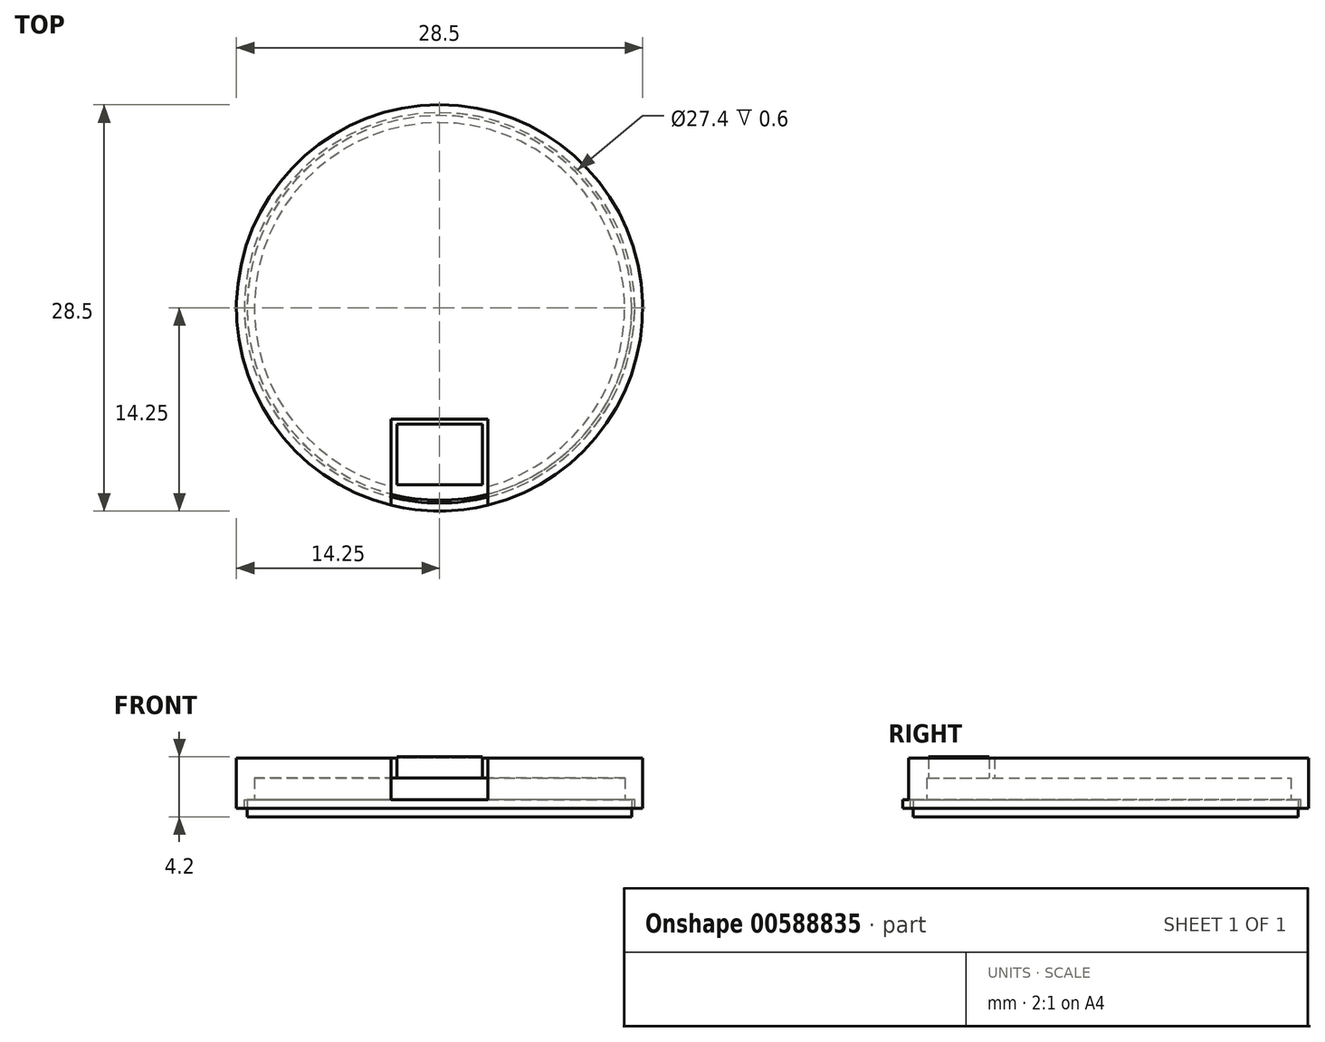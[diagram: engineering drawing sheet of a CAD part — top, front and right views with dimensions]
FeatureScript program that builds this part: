
annotation { "Feature Type Name" : "Feature", "Feature Type Description" : "" }
export const myFeature = defineFeature(function(context is Context, id is Id, definition is map)
    precondition{}
    {
        {
            var Q0;
            Q0=qCreatedBy(makeId("Top.planeOp"),FACE);
            var sketch = newSketch(context, id + "F0", { "sketchPlane" : qUnion([Q0])});
            skCircle(sketch, "E0", {"center": v(0, 0) * mm, "radius": 13.5 * mm});
            skLineSegment(sketch, "E1.bottom", {"start": v(3, -12.42) * mm, "end": v(-3, -12.42) * mm});
            skLineSegment(sketch, "E1.top", {"start": v(3, -8.17) * mm, "end": v(-3, -8.17) * mm});
            skLineSegment(sketch, "E1.left", {"start": v(3, -12.42) * mm, "end": v(3, -8.17) * mm});
            skLineSegment(sketch, "E1.right", {"start": v(-3, -12.42) * mm, "end": v(-3, -8.17) * mm});
            skPoint(sketch, "E1.middle", {"position": v(0, -10.3) * mm});
            skSolve(sketch);
        }
        {
            var Q0;
            Q0 = qSketchRegion(id + "F0", true);
            var Q1;
            Q1=makeQuery(id+"F0.imprint","IMPRINT",FACE,{"disambiguationData":[TD([[makeQuery(id+"F0.imprint","IMPRINT",EDGE,{"derivedFrom":sQuery(id+"F0.wireOp",EDGE,"E1.bottom")}),-1.0]])]});
            extrude(context, id + "F1", {"entities" : qUnion([Q0, Q1]), "depth" : 1.2 * mm, "offsetDistance" : 25 * mm});
        }
        {
            var Q0;
            Q0=makeQuery(id+"F0.imprint","IMPRINT",FACE,{"disambiguationData":[TD([[makeQuery(id+"F0.imprint","IMPRINT",EDGE,{"derivedFrom":sQuery(id+"F0.wireOp",EDGE,"E1.bottom")}),-1.0]])]});
            extrude(context, id + "F2", {"entities" : qUnion([Q0]), "operationType" : NewBodyOperationType.ADD, "depth" : 4.2 * mm, "offsetDistance" : 25 * mm});
        }
        {
            var Q0;
            Q0=makeQuery(id+"F1.opExtrude","CAP_FACE",FACE,{"disambiguationData":[OSD([sQuery(id+"F0.wireOp",EDGE,"E0")])],"isStart":false});
            var sketch = newSketch(context, id + "F3", { "sketchPlane" : qUnion([Q0])});
            skCircle(sketch, "E2", {"center": v(0, 0) * mm, "radius": 14.25 * mm});
            skCircle(sketch, "E3", {"center": v(0, 0) * mm, "radius": 13.7 * mm});
            skLineSegment(sketch, "E4.bottom", {"start": v(3.4, -12.8) * mm, "end": v(-3.4, -12.8) * mm});
            skLineSegment(sketch, "E4.top", {"start": v(3.4, -7.8) * mm, "end": v(-3.4, -7.8) * mm});
            skLineSegment(sketch, "E4.left", {"start": v(3.4, -12.8) * mm, "end": v(3.4, -7.8) * mm});
            skLineSegment(sketch, "E4.right", {"start": v(-3.4, -12.8) * mm, "end": v(-3.4, -7.8) * mm});
            skPoint(sketch, "E4.middle", {"position": v(0, -10.3) * mm});
            skCircle(sketch, "E5", {"center": v(0, 0) * mm, "radius": 13 * mm});
            skSolve(sketch);
        }
        {
            var Q0;
            {var subQ0=sQuery(id+"F3.wireOp",EDGE,"E4.top");Q0=makeQuery(id+"F3.imprint","IMPRINT",FACE,{"disambiguationData":[TD([[makeQuery(id+"F3.imprint","IMPRINT",EDGE,{"derivedFrom":subQ0}),-1.0]])]});}
            var Q1;
            Q1=makeQuery(id+"F3.imprint","IMPRINT",FACE,{"disambiguationData":[TD([[makeQuery(id+"F3.imprint","IMPRINT",EDGE,{"derivedFrom":makeQuery(id+"F1.opExtrude","CAP_EDGE",EDGE,{"disambiguationData":[OSD([sQuery(id+"F0.wireOp",EDGE,"E0")])],"isStart":false})}),1.0]])]});
            var Q2;
            {var subQ0=sQuery(id+"F3.wireOp",EDGE,"E5");var subQ1=sQuery(id+"F3.wireOp",EDGE,"E4.bottom");var subQ2=makeQuery(id+"F3.imprint","INTERSECT",VERTEX,{"disambiguationData":[OD(0.0)],"derivedFrom":[subQ1,subQ0]});Q2=makeQuery(id+"F3.imprint","IMPRINT",FACE,{"disambiguationData":[TD([[makeQuery(id+"F3.imprint","IMPRINT",EDGE,{"disambiguationData":[TD([[subQ2,-1.0]])],"derivedFrom":subQ1}),1.0]])]});}
            var Q3;
            Q3=makeQuery(id+"F3.imprint","IMPRINT",FACE,{"disambiguationData":[TD([[makeQuery(id+"F3.imprint","IMPRINT",EDGE,{"derivedFrom":sQuery(id+"F3.wireOp",EDGE,"E3")}),1.0]])]});
            var Q4;
            Q4=makeQuery(id+"F3.imprint","IMPRINT",FACE,{"disambiguationData":[TD([[makeQuery(id+"F3.imprint","IMPRINT",EDGE,{"derivedFrom":sQuery(id+"F3.wireOp",EDGE,"E2")}),1.0]])]});
            extrude(context, id + "F4", {"entities" : qUnion([Q0, Q1, Q2, Q3, Q4]), "depth" : 2.9 * mm, "offsetDistance" : 25 * mm});
        }
        {
            var Q0;
            Q0=makeQuery(id+"F3.imprint","IMPRINT",FACE,{"disambiguationData":[TD([[makeQuery(id+"F3.imprint","IMPRINT",EDGE,{"derivedFrom":sQuery(id+"F3.wireOp",EDGE,"E2")}),1.0]])]});
            extrude(context, id + "F5", {"entities" : qUnion([Q0]), "operationType" : NewBodyOperationType.ADD, "oppositeDirection" : true, "depth" : 0.6 * mm, "offsetDistance" : 25 * mm});
        }
        {
            var Q0;
            {var subQ0=sQuery(id+"F3.wireOp",EDGE,"E4.top");Q0=makeQuery(id+"F3.imprint","IMPRINT",FACE,{"disambiguationData":[TD([[makeQuery(id+"F3.imprint","IMPRINT",EDGE,{"derivedFrom":subQ0}),-1.0]])]});}
            var Q1;
            {var subQ1=sQuery(id+"F3.wireOp",EDGE,"E4.top");Q1=makeQuery(id+"F3.imprint","IMPRINT",FACE,{"disambiguationData":[TD([[makeQuery(id+"F3.imprint","IMPRINT",EDGE,{"derivedFrom":subQ1}),1.0]])]});}
            var Q2;
            {var subQ0=sQuery(id+"F3.wireOp",EDGE,"E5");var subQ1=sQuery(id+"F3.wireOp",EDGE,"E4.bottom");var subQ2=makeQuery(id+"F3.imprint","INTERSECT",VERTEX,{"disambiguationData":[OD(0.0)],"derivedFrom":[subQ1,subQ0]});Q2=makeQuery(id+"F3.imprint","IMPRINT",FACE,{"disambiguationData":[TD([[makeQuery(id+"F3.imprint","IMPRINT",EDGE,{"disambiguationData":[TD([[subQ2,-1.0]])],"derivedFrom":subQ1}),1.0]])]});}
            var Q3;
            {var subQ0=makeQuery(id+"F1.opExtrude","CAP_FACE",FACE,{"disambiguationData":[OSD([sQuery(id+"F0.wireOp",EDGE,"E0")])],"isStart":false});Q3=makeQuery(id+"F3.imprint","IMPRINT",FACE,{"disambiguationData":[TD([[makeQuery(id+"F3.imprint","IMPRINT",EDGE,{"derivedFrom":makeQuery(id+"F2.boolean.opBoolean","INTERSECT",EDGE,{"derivedFrom":[subQ0,makeQuery(id+"F2.opExtrude","SWEPT_FACE",FACE,{"disambiguationData":[OSD([sQuery(id+"F0.wireOp",EDGE,"E1.bottom")])]})]})}),1.0]])]});}
            var Q4;
            Q4=sQuery(id+"F3.wireOp",EDGE,"E5");
            extrude(context, id + "F6", {"entities" : qUnion([Q0, Q1, Q2, Q3]), "operationType" : NewBodyOperationType.REMOVE, "surfaceEntities" : qUnion([Q4]), "depth" : 1.5 * mm, "offsetDistance" : 25 * mm});
        }
        {
            var Q0;
            Q0=makeQuery(id+"F2.opExtrude","SWEPT_FACE",FACE,{"disambiguationData":[OSD([sQuery(id+"F0.wireOp",EDGE,"E1.bottom")])]});
            var sketch = newSketch(context, id + "F7", { "sketchPlane" : qUnion([Q0])});
            skLineSegment(sketch, "E6.bottom", {"start": v(-3.4, 4.2) * mm, "end": v(3.4, 4.2) * mm});
            skLineSegment(sketch, "E6.top", {"start": v(-3.4, 1.2) * mm, "end": v(3.4, 1.2) * mm});
            skLineSegment(sketch, "E6.left", {"start": v(-3.4, 4.2) * mm, "end": v(-3.4, 1.2) * mm});
            skLineSegment(sketch, "E6.right", {"start": v(3.4, 4.2) * mm, "end": v(3.4, 1.2) * mm});
            skSolve(sketch);
        }
        {
            var Q0;
            Q0 = qSketchRegion(id + "F7", true);
            extrude(context, id + "F8", {"entities" : qUnion([Q0]), "operationType" : NewBodyOperationType.REMOVE, "depth" : 8 * mm, "offsetDistance" : 25 * mm});
        }
    });
